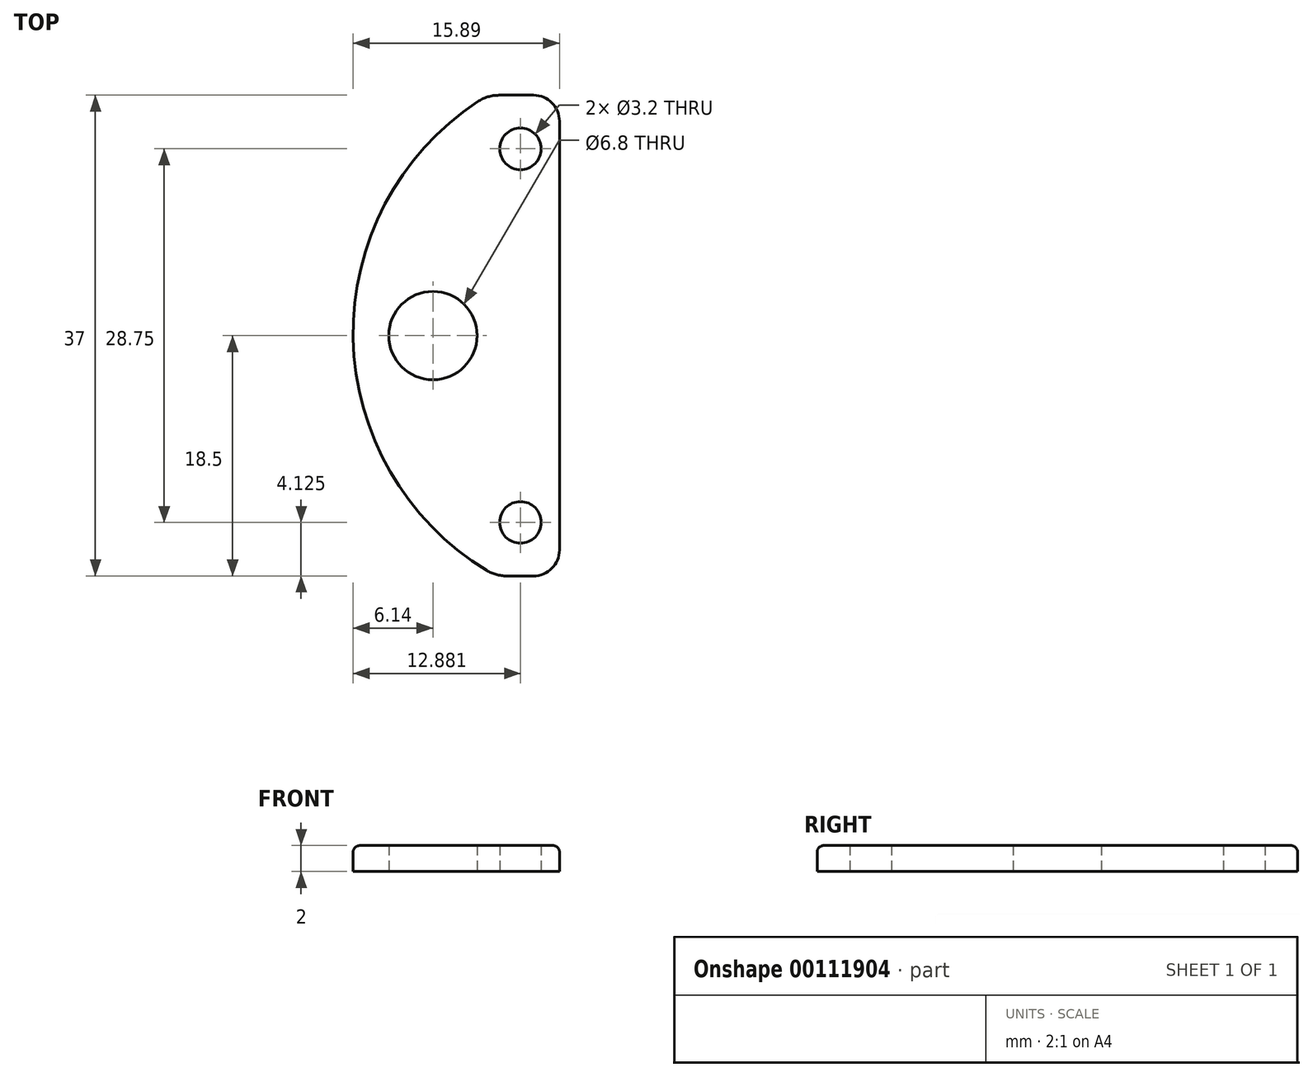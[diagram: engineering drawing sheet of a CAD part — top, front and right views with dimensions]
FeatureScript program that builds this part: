
annotation { "Feature Type Name" : "Feature", "Feature Type Description" : "" }
export const myFeature = defineFeature(function(context is Context, id is Id, definition is map)
    precondition{}
    {
        {
            var Q0;
            Q0=qCreatedBy(makeId("Top.planeOp"),FACE);
            var sketch = newSketch(context, id + "F0", { "sketchPlane" : qUnion([Q0])});
            skLineSegment(sketch, "E0.bottom", {"start": v(12.93, -18.5) * mm, "end": v(15, -18.5) * mm});
            skLineSegment(sketch, "E0.top", {"start": v(12.34, 18.5) * mm, "end": v(15, 18.5) * mm});
            skLineSegment(sketch, "E0.right", {"start": v(17, -16.5) * mm, "end": v(17, 16.5) * mm});
            skPoint(sketch, "E0.middle", {"position": v(0, 0) * mm});
            skLineSegment(sketch, "E1.bottom", {"start": v(6.84, -14.37) * mm, "end": v(14, -14.37) * mm, "construction": true});
            skLineSegment(sketch, "E1.top", {"start": v(6.5, 14.37) * mm, "end": v(14, 14.37) * mm, "construction": true});
            skLineSegment(sketch, "E1.right", {"start": v(14, -14.37) * mm, "end": v(14, 14.37) * mm, "construction": true});
            skCircle(sketch, "E2", {"center": v(14, -14.37) * mm, "radius": 1.6 * mm});
            skCircle(sketch, "E3.MirrorC", {"center": v(14, 14.37) * mm, "radius": 1.6 * mm});
            skPoint(sketch, "E4.endSnap0", {"position": v(17, 0) * mm});
            skCircle(sketch, "E5", {"center": v(7.25, 0) * mm, "radius": 3.4 * mm});
            skPoint(sketch, "E6.visualSharp", {"position": v(17, 18.5) * mm});
            skArc(sketch, "E6.filletArc", {"start": v(17, 16.5) * mm, "mid": v(16.41, 17.91) * mm, "end": v(15, 18.5) * mm});
            skPoint(sketch, "E7.visualSharp", {"position": v(-17, -18.5) * mm});
            skPoint(sketch, "E8.visualSharp", {"position": v(17, -18.5) * mm});
            skArc(sketch, "E8.filletArc", {"start": v(15, -18.5) * mm, "mid": v(16.41, -17.91) * mm, "end": v(17, -16.5) * mm});
            skArc(sketch, "E9", {"start": v(10.69, 18) * mm, "mid": v(1.1, -0.22) * mm, "end": v(11.37, -18.06) * mm});
            skPoint(sketch, "E9.endSnap0", {"position": v(12.12, 0) * mm});
            skPoint(sketch, "E10.orphan", {"position": v(-14, 14.37) * mm});
            skPoint(sketch, "E11.orphan", {"position": v(-14, -14.37) * mm});
            skPoint(sketch, "E12.visualSharp", {"position": v(11.48, 18.5) * mm});
            skArc(sketch, "E12.filletArc", {"start": v(12.34, 18.5) * mm, "mid": v(11.48, 18.37) * mm, "end": v(10.69, 18) * mm});
            skPoint(sketch, "E13.visualSharp", {"position": v(12.12, -18.5) * mm});
            skArc(sketch, "E13.filletArc", {"start": v(11.37, -18.06) * mm, "mid": v(12.12, -18.39) * mm, "end": v(12.93, -18.5) * mm});
            skSolve(sketch);
        }
        {
            var Q0;
            Q0=makeQuery(id+"F0.imprint","IMPRINT",FACE,{"disambiguationData":[TD([[makeQuery(id+"F0.imprint","IMPRINT",EDGE,{"derivedFrom":sQuery(id+"F0.wireOp",EDGE,"E0.bottom")}),1.0]])]});
            extrude(context, id + "F1", {"entities" : qUnion([Q0]), "depth" : 2 * mm});
        }
        {
            var Q0;
            Q0=makeQuery(id+"F1.opExtrude","CAP_EDGE",EDGE,{"disambiguationData":[OSD([sQuery(id+"F0.wireOp",EDGE,"E9")])],"isStart":false});
            fillet(context, id + "F2", {"entities" : qUnion([Q0]), "radius" : .5 * mm, "tangentPropagation" : true, "allowEdgeOverflow" : false});
        }
    });
